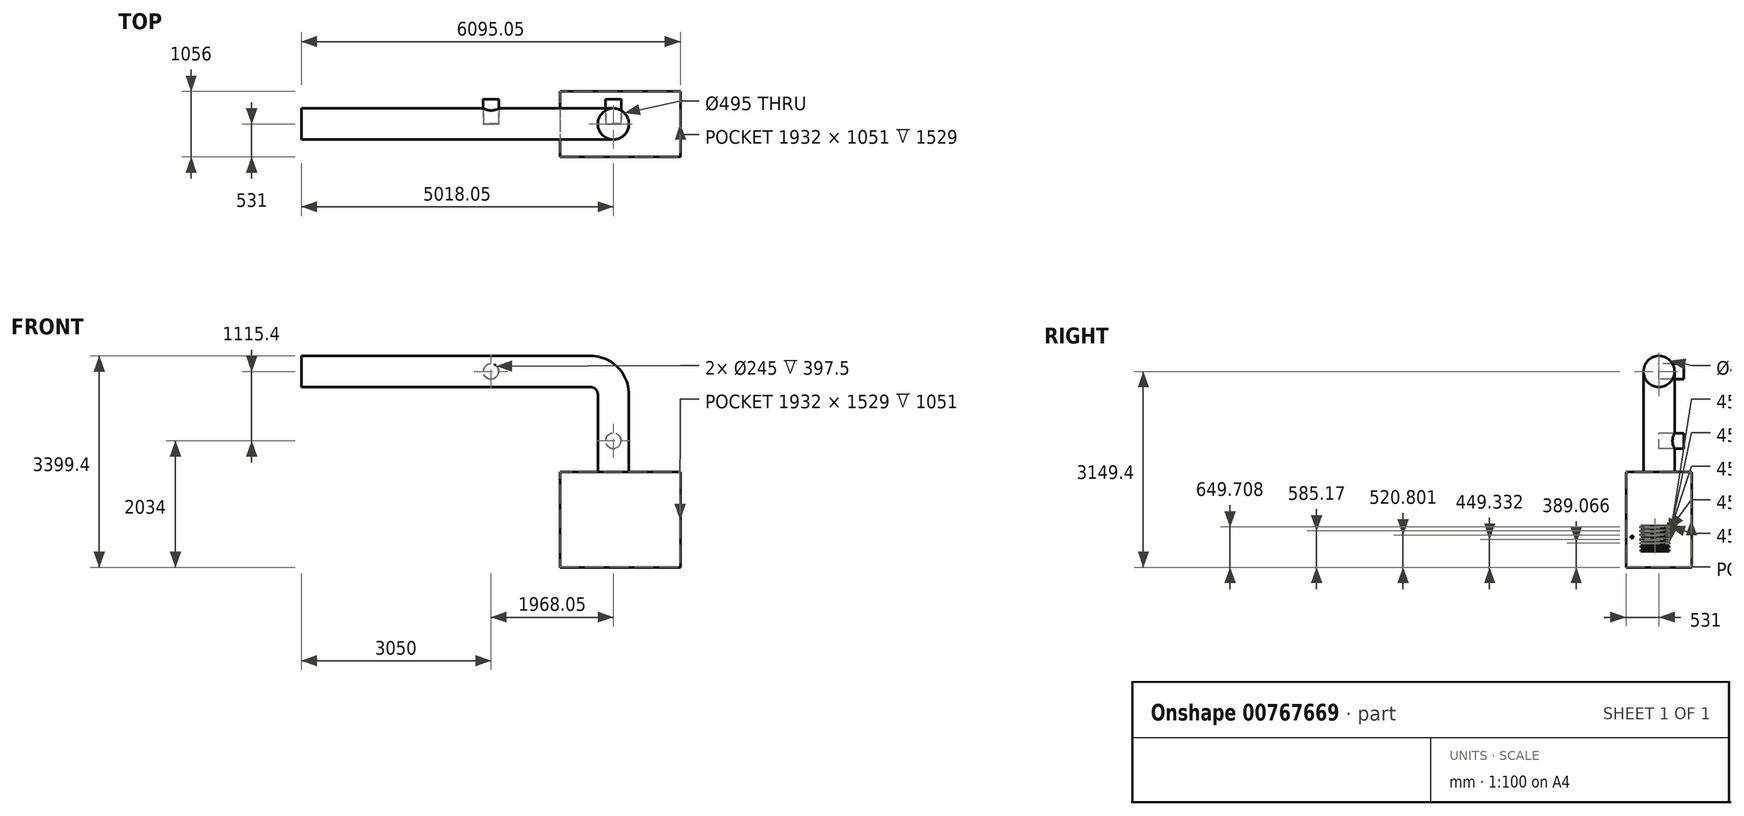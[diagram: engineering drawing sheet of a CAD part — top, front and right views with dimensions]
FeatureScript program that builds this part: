
annotation { "Feature Type Name" : "Feature", "Feature Type Description" : "" }
export const myFeature = defineFeature(function(context is Context, id is Id, definition is map)
    precondition{}
    {
        {
            var Q0;
            Q0=qCreatedBy(makeId("Top.planeOp"),FACE);
            var sketch = newSketch(context, id + "F0", { "sketchPlane" : qUnion([Q0])});
            skLineSegment(sketch, "E0.bottom", {"start": v(-968.5, 528) * mm, "end": v(968.5, 528) * mm});
            skLineSegment(sketch, "E0.top", {"start": v(-968.5, -528) * mm, "end": v(968.5, -528) * mm});
            skLineSegment(sketch, "E0.left", {"start": v(-968.5, 528) * mm, "end": v(-968.5, -528) * mm});
            skLineSegment(sketch, "E0.right", {"start": v(968.5, 528) * mm, "end": v(968.5, -528) * mm});
            skSolve(sketch);
        }
        {
            var Q0;
            Q0=makeQuery(id+"F0.imprint","IMPRINT",FACE,{"disambiguationData":[TD([[makeQuery(id+"F0.imprint","IMPRINT",EDGE,{"derivedFrom":sQuery(id+"F0.wireOp",EDGE,"E0.bottom")}),-1.0]])]});
            extrude(context, id + "F1", {"entities" : qUnion([Q0]), "depth" : 1534 * mm, "offsetDistance" : 25 * mm});
        }
        {
            var Q0;
            Q0=makeQuery(id+"F1.opExtrude","SWEPT_FACE",FACE,{"disambiguationData":[OSD([sQuery(id+"F0.wireOp",EDGE,"E0.right")])]});
            var sketch = newSketch(context, id + "F2", { "sketchPlane" : qUnion([Q0])});
            skLineSegment(sketch, "E1.bottom", {"start": v(-288.2, 709) * mm, "end": v(168.8, 709) * mm});
            skLineSegment(sketch, "E1.top", {"start": v(-288.2, 225) * mm, "end": v(168.8, 225) * mm});
            skLineSegment(sketch, "E1.left", {"start": v(-288.2, 709) * mm, "end": v(-288.2, 225) * mm});
            skLineSegment(sketch, "E1.right", {"start": v(168.8, 709) * mm, "end": v(168.8, 225) * mm});
            skLineSegment(sketch, "E2.bottom", {"start": v(-288.2, 663.92) * mm, "end": v(168.8, 663.92) * mm});
            skLineSegment(sketch, "E2.top", {"start": v(-288.2, 635.5) * mm, "end": v(168.8, 635.5) * mm});
            skLineSegment(sketch, "E2.left", {"start": v(-288.2, 663.92) * mm, "end": v(-288.2, 635.5) * mm});
            skLineSegment(sketch, "E2.right", {"start": v(168.8, 663.92) * mm, "end": v(168.8, 635.5) * mm});
            skLineSegment(sketch, "E3.bottom", {"start": v(-288.2, 600.62) * mm, "end": v(168.8, 600.62) * mm});
            skLineSegment(sketch, "E3.top", {"start": v(-288.2, 569.72) * mm, "end": v(168.8, 569.72) * mm});
            skLineSegment(sketch, "E3.left", {"start": v(-288.2, 600.62) * mm, "end": v(-288.2, 569.72) * mm});
            skLineSegment(sketch, "E3.right", {"start": v(168.8, 600.62) * mm, "end": v(168.8, 569.72) * mm});
            skLineSegment(sketch, "E4.bottom", {"start": v(-288.2, 534.66) * mm, "end": v(168.8, 534.66) * mm});
            skLineSegment(sketch, "E4.top", {"start": v(-288.2, 506.94) * mm, "end": v(168.8, 506.94) * mm});
            skLineSegment(sketch, "E4.left", {"start": v(-288.2, 534.66) * mm, "end": v(-288.2, 506.94) * mm});
            skLineSegment(sketch, "E4.right", {"start": v(168.8, 534.66) * mm, "end": v(168.8, 506.94) * mm});
            skLineSegment(sketch, "E5.bottom", {"start": v(-288.2, 467) * mm, "end": v(168.8, 467) * mm});
            skLineSegment(sketch, "E5.top", {"start": v(-288.2, 431.66) * mm, "end": v(168.8, 431.66) * mm});
            skLineSegment(sketch, "E5.left", {"start": v(-288.2, 467) * mm, "end": v(-288.2, 431.66) * mm});
            skLineSegment(sketch, "E5.right", {"start": v(168.8, 467) * mm, "end": v(168.8, 431.66) * mm});
            skLineSegment(sketch, "E6.bottom", {"start": v(-288.2, 399.83) * mm, "end": v(168.8, 399.83) * mm});
            skLineSegment(sketch, "E6.top", {"start": v(-288.2, 378.3) * mm, "end": v(168.8, 378.3) * mm});
            skLineSegment(sketch, "E6.left", {"start": v(-288.2, 399.83) * mm, "end": v(-288.2, 378.3) * mm});
            skLineSegment(sketch, "E6.right", {"start": v(168.8, 399.83) * mm, "end": v(168.8, 378.3) * mm});
            skLineSegment(sketch, "E7.bottom", {"start": v(-288.2, 343.56) * mm, "end": v(168.8, 343.56) * mm});
            skLineSegment(sketch, "E7.top", {"start": v(-288.2, 318.6) * mm, "end": v(168.8, 318.6) * mm});
            skLineSegment(sketch, "E7.left", {"start": v(-288.2, 343.56) * mm, "end": v(-288.2, 318.6) * mm});
            skLineSegment(sketch, "E7.right", {"start": v(168.8, 343.56) * mm, "end": v(168.8, 318.6) * mm});
            skLineSegment(sketch, "E8.bottom", {"start": v(-288.2, 280.6) * mm, "end": v(168.8, 280.6) * mm});
            skLineSegment(sketch, "E8.top", {"start": v(-288.2, 255.83) * mm, "end": v(168.8, 255.83) * mm});
            skLineSegment(sketch, "E8.left", {"start": v(-288.2, 280.6) * mm, "end": v(-288.2, 255.83) * mm});
            skLineSegment(sketch, "E8.right", {"start": v(168.8, 280.6) * mm, "end": v(168.8, 255.83) * mm});
            skSolve(sketch);
        }
        {
            var Q0;
            Q0=makeQuery(id+"F1.opExtrude","SWEPT_FACE",FACE,{"disambiguationData":[OSD([sQuery(id+"F0.wireOp",EDGE,"E0.top")])]});
            cPlane(context, id + "F3", {"entities" : qUnion([Q0]), "cplaneType" : CPlaneType.OFFSET, "offset" : (239.8 + (457 / 2)) * mm, "oppositeDirection" : true, "width" : 150 * mm, "height" : 150 * mm});
        }
        {
            var Q0;
            Q0=makeQuery(id+"F1.opExtrude","CAP_FACE",FACE,{"disambiguationData":[OSD([sQuery(id+"F0.wireOp",EDGE,"E0.bottom"),sQuery(id+"F0.wireOp",EDGE,"E0.top"),sQuery(id+"F0.wireOp",EDGE,"E0.left"),sQuery(id+"F0.wireOp",EDGE,"E0.right")])],"isStart":false});
            var sketch = newSketch(context, id + "F4", { "sketchPlane" : qUnion([Q0])});
            skLineSegment(sketch, "E9.bottom", {"start": v(42.1, -416) * mm, "end": v(-295.2, -416) * mm});
            skLineSegment(sketch, "E9.top", {"start": v(42.1, 420) * mm, "end": v(-295.2, 420) * mm});
            skLineSegment(sketch, "E9.left", {"start": v(42.1, -416) * mm, "end": v(42.1, 420) * mm});
            skLineSegment(sketch, "E9.right", {"start": v(-295.2, -416) * mm, "end": v(-295.2, 420) * mm});
            skCircle(sketch, "E10", {"center": v(-108.5, 3) * mm, "radius": 250 * mm});
            skSolve(sketch);
        }
        {
            var Q0;
            Q0=makeQuery(id+"F1.opExtrude","SWEPT_FACE",FACE,{"disambiguationData":[OSD([sQuery(id+"F0.wireOp",EDGE,"E0.top")])]});
            cPlane(context, id + "F5", {"entities" : qUnion([Q0]), "cplaneType" : CPlaneType.OFFSET, "offset" : (112 + (836 / 2)) * mm, "oppositeDirection" : true, "width" : 150 * mm, "height" : 150 * mm});
        }
        {
            var Q0;
            Q0=qCreatedBy(id+"F3.planeOp",FACE);
            var sketch = newSketch(context, id + "F6", { "sketchPlane" : qUnion([Q0])});
            skPoint(sketch, "E11.0", {"position": v(-126.55, 1534) * mm});
            skLineSegment(sketch, "E12", {"start": v(-126.55, 1534) * mm, "end": v(-126.55, 2781.35) * mm});
            skLineSegment(sketch, "E13", {"start": v(-476.55, 3131.35) * mm, "end": v(-5126.55, 3131.35) * mm});
            skPoint(sketch, "E14.visualSharp", {"position": v(-126.55, 3131.35) * mm});
            skArc(sketch, "E14.filletArc", {"start": v(-126.55, 2781.35) * mm, "mid": v(-229.07, 3028.84) * mm, "end": v(-476.55, 3131.35) * mm});
            skSolve(sketch);
        }
        {
            var Q0;
            {var subQ0=sQuery(id+"F4.wireOp",EDGE,"E10");var subQ1=sQuery(id+"F4.wireOp",EDGE,"E9.left");var subQ2=makeQuery(id+"F4.imprint","INTERSECT",VERTEX,{"disambiguationData":[OD(0.0)],"derivedFrom":[subQ1,subQ0]});Q0=makeQuery(id+"F4.imprint","IMPRINT",FACE,{"disambiguationData":[TD([[makeQuery(id+"F4.imprint","IMPRINT",EDGE,{"disambiguationData":[TD([[subQ2,-1.0]])],"derivedFrom":subQ1}),1.0]])]});}
            var Q1;
            {var subQ0=sQuery(id+"F4.wireOp",EDGE,"E10");var subQ1=sQuery(id+"F4.wireOp",EDGE,"E9.right");var subQ2=makeQuery(id+"F4.imprint","INTERSECT",VERTEX,{"disambiguationData":[OD(0.0)],"derivedFrom":[subQ1,subQ0]});Q1=makeQuery(id+"F4.imprint","IMPRINT",FACE,{"disambiguationData":[TD([[makeQuery(id+"F4.imprint","IMPRINT",EDGE,{"disambiguationData":[TD([[subQ2,-1.0]])],"derivedFrom":subQ1}),1.0]])]});}
            var Q2;
            {var subQ0=sQuery(id+"F4.wireOp",EDGE,"E10");var subQ1=sQuery(id+"F4.wireOp",EDGE,"E9.left");var subQ2=makeQuery(id+"F4.imprint","INTERSECT",VERTEX,{"disambiguationData":[OD(0.0)],"derivedFrom":[subQ1,subQ0]});Q2=makeQuery(id+"F4.imprint","IMPRINT",FACE,{"disambiguationData":[TD([[makeQuery(id+"F4.imprint","IMPRINT",EDGE,{"disambiguationData":[TD([[subQ2,-1.0]])],"derivedFrom":subQ1}),-1.0]])]});}
            var Q3;
            Q3=sQuery(id+"F6.wireOp",EDGE,"E12");
            var Q4;
            Q4=sQuery(id+"F6.wireOp",EDGE,"E13");
            var Q5;
            Q5=sQuery(id+"F6.wireOp",EDGE,"E14.filletArc");
            sweep(context, id + "F7", {"operationType" : NewBodyOperationType.ADD, "profiles" : qUnion([Q0, Q1, Q2]), "path" : qUnion([Q3, Q4, Q5])});
        }
        {
            var Q0;
            Q0=makeQuery(id+"F7.opSweep","CAP_FACE",FACE,{"disambiguationData":[OSD([sQuery(id+"F4.wireOp",EDGE,"E9.bottom"),sQuery(id+"F4.wireOp",EDGE,"E9.top"),sQuery(id+"F4.wireOp",EDGE,"E9.left"),sQuery(id+"F4.wireOp",EDGE,"E9.right"),sQuery(id+"F6.wireOp",VERTEX,"E13.end")])],"isStart":false});
            shell(context, id + "F8", {"entities" : qUnion([Q0]), "thickness" : 2.5 * mm});
        }
        {
            var Q0;
            Q0=makeQuery(id+"F1.opExtrude","SWEPT_FACE",FACE,{"disambiguationData":[OSD([sQuery(id+"F0.wireOp",EDGE,"E0.right")])]});
            var sketch = newSketch(context, id + "F9", { "sketchPlane" : qUnion([Q0])});
            skCircle(sketch, "E15", {"center": v(-430, 487) * mm, "radius": 19.05 * mm});
            skSolve(sketch);
        }
        {
            var Q0;
            Q0=makeQuery(id+"F9.imprint","IMPRINT",FACE,{"disambiguationData":[TD([[makeQuery(id+"F9.imprint","IMPRINT",EDGE,{"derivedFrom":sQuery(id+"F9.wireOp",EDGE,"E15")}),1.0]])]});
            extrude(context, id + "F10", {"entities" : qUnion([Q0]), "operationType" : NewBodyOperationType.REMOVE, "oppositeDirection" : true, "depth" : 25 * mm, "offsetDistance" : 25 * mm});
        }
        {
            var Q0;
            {var subQ0=sQuery(id+"F2.wireOp",EDGE,"E2.bottom");Q0=makeQuery(id+"F2.imprint","IMPRINT",FACE,{"disambiguationData":[TD([[makeQuery(id+"F2.imprint","IMPRINT",EDGE,{"derivedFrom":subQ0}),-1.0]])]});}
            var Q1;
            {var subQ0=sQuery(id+"F2.wireOp",EDGE,"E3.bottom");Q1=makeQuery(id+"F2.imprint","IMPRINT",FACE,{"disambiguationData":[TD([[makeQuery(id+"F2.imprint","IMPRINT",EDGE,{"derivedFrom":subQ0}),-1.0]])]});}
            var Q2;
            {var subQ0=sQuery(id+"F2.wireOp",EDGE,"E4.bottom");Q2=makeQuery(id+"F2.imprint","IMPRINT",FACE,{"disambiguationData":[TD([[makeQuery(id+"F2.imprint","IMPRINT",EDGE,{"derivedFrom":subQ0}),-1.0]])]});}
            var Q3;
            {var subQ0=sQuery(id+"F2.wireOp",EDGE,"E5.bottom");Q3=makeQuery(id+"F2.imprint","IMPRINT",FACE,{"disambiguationData":[TD([[makeQuery(id+"F2.imprint","IMPRINT",EDGE,{"derivedFrom":subQ0}),-1.0]])]});}
            var Q4;
            {var subQ2=sQuery(id+"F2.wireOp",EDGE,"E6.bottom");Q4=makeQuery(id+"F2.imprint","IMPRINT",FACE,{"disambiguationData":[TD([[makeQuery(id+"F2.imprint","IMPRINT",EDGE,{"derivedFrom":subQ2}),-1.0]])]});}
            var Q5;
            {var subQ0=sQuery(id+"F2.wireOp",EDGE,"E7.bottom");Q5=makeQuery(id+"F2.imprint","IMPRINT",FACE,{"disambiguationData":[TD([[makeQuery(id+"F2.imprint","IMPRINT",EDGE,{"derivedFrom":subQ0}),-1.0]])]});}
            var Q6;
            {var subQ0=sQuery(id+"F2.wireOp",EDGE,"E8.bottom");Q6=makeQuery(id+"F2.imprint","IMPRINT",FACE,{"disambiguationData":[TD([[makeQuery(id+"F2.imprint","IMPRINT",EDGE,{"derivedFrom":subQ0}),-1.0]])]});}
            extrude(context, id + "F11", {"entities" : qUnion([Q0, Q1, Q2, Q3, Q4, Q5, Q6]), "operationType" : NewBodyOperationType.REMOVE, "oppositeDirection" : true, "depth" : 25 * mm, "offsetDistance" : 25 * mm});
        }
        {
            var Q0;
            Q0=qCreatedBy(id+"F5.planeOp",FACE);
            var sketch = newSketch(context, id + "F12", { "sketchPlane" : qUnion([Q0])});
            skCircle(sketch, "E16", {"center": v(-108.5, 2034) * mm, "radius": 125 * mm});
            skLineSegment(sketch, "E17", {"start": v(141.5, 2781.35) * mm, "end": v(141.5, 1534) * mm, "construction": true});
            skLineSegment(sketch, "E18", {"start": v(-358.5, 1534) * mm, "end": v(-358.5, 2781.35) * mm, "construction": true});
            skCircle(sketch, "E19", {"center": v(-2076.55, 3149.4) * mm, "radius": 125 * mm});
            skLineSegment(sketch, "E20", {"start": v(-476.55, 2899.4) * mm, "end": v(-5126.55, 2899.4) * mm});
            skLineSegment(sketch, "E21.0", {"start": v(-476.55, 2899.4) * mm, "end": v(-476.55, 3399.4) * mm});
            skSolve(sketch);
        }
        {
            var Q0;
            Q0 = qSketchRegion(id + "F12", true);
            extrude(context, id + "F13", {"entities" : qUnion([Q0]), "operationType" : NewBodyOperationType.ADD, "oppositeDirection" : true, "depth" : 400 * mm, "offsetDistance" : 25 * mm});
        }
        {
            var Q0;
            Q0=makeQuery(id+"F13.opExtrude","CAP_FACE",FACE,{"disambiguationData":[OSD([sQuery(id+"F12.wireOp",EDGE,"E16")])],"isStart":false});
            var Q1;
            Q1=makeQuery(id+"F13.opExtrude","CAP_FACE",FACE,{"disambiguationData":[OSD([sQuery(id+"F12.wireOp",EDGE,"E19")])],"isStart":false});
            shell(context, id + "F14", {"entities" : qUnion([Q0, Q1]), "thickness" : 2.5 * mm});
        }
    });
